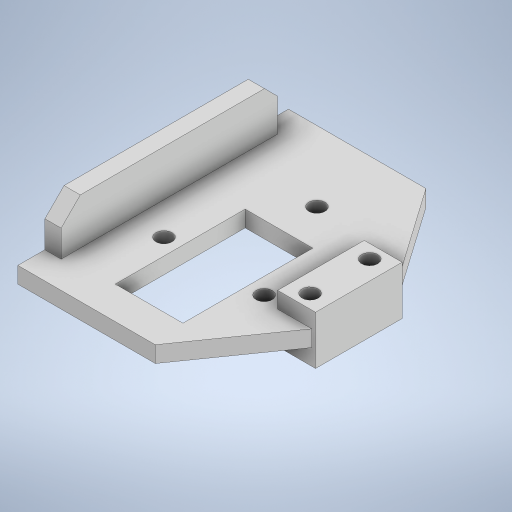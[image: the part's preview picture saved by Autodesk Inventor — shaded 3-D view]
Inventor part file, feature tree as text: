
AUTODESK INVENTOR PART (.ipt)
format: ipt  version: 2023 (Build 270158000, 158)  size: 325,120 bytes
history: native  units: mm
features: extrude x5, sketch x5, other x1
ambient origin geometry x8: Origin, YZ Plane, XZ Plane, XY Plane, X Axis, Y Axis, Z Axis, Center Point
bodies: Body1 (feature_tree)
feature tree (11):
  other  "Sólido1"
  extrude  "Extrusión1"  TaperAngle=135.0deg  [1 undecoded]
  extrude  "Extrusión2"  Depth=40.0mm
  extrude  "Extrusión3"  Depth=3.0mm TaperAngle=0.0deg
  extrude  "Extrusión4"  Depth=38.0mm
  extrude  "Extrusión5"  Depth=1.0mm
  sketch  "Boceto1"  dims[d0=135.0deg d2=135.0deg]
  sketch  "Boceto2"  dims[d3=135.0deg d5=40.0mm]
  sketch  "Boceto3"  dims[d6=20.0mm d7=3.0mm d8=0.0mm]
  sketch  "Boceto4"  dims[d9=50.0mm d10=38.0mm]
  sketch  "Boceto5"  dims[d11=25.307274mm d12=25.307274mm d13=12.5mm d14=24.0mm d15=6.0mm d16=12.0mm d17=3.0mm d18=3.0mm d19=3.0mm d20=3.0mm d21=3.0mm d22=7.0mm d23=3.0mm d24=0.0mm d25=7.0mm d26=9.0mm d27=0.0mm d28=3.0mm d29=3.0mm d30=11.0mm d31=5.5mm d34=8.0mm d35=8.0mm d36=9.0mm d37=0.0mm d38=7.0mm d39=1.0mm d40=0.0mm]
note: 1 required parameter value undecoded (feature->parameter linkage not recoverable at this tier; creation-order binding heuristic only, values carry confidence <= 0.55)
